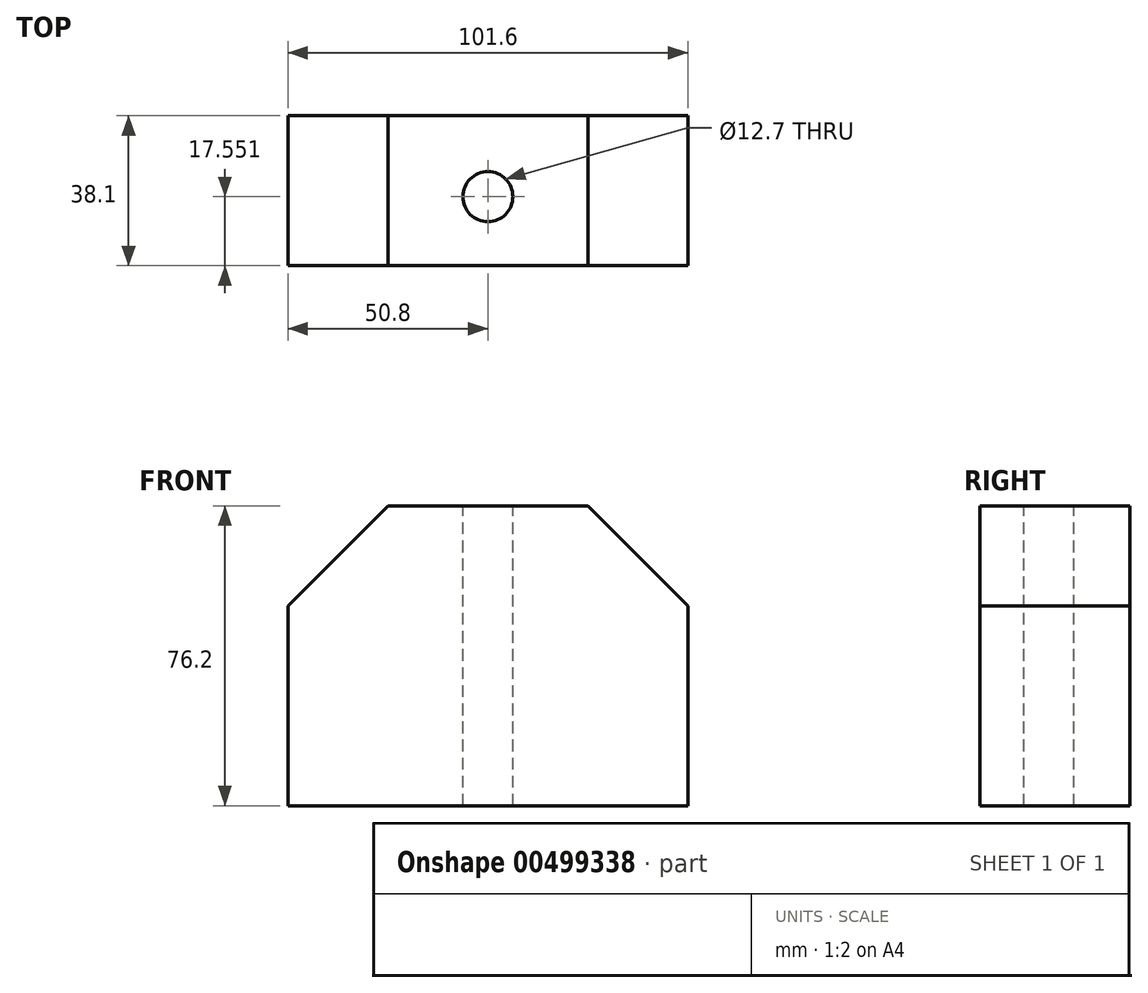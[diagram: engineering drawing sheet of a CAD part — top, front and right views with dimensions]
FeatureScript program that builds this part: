
annotation { "Feature Type Name" : "Feature", "Feature Type Description" : "" }
export const myFeature = defineFeature(function(context is Context, id is Id, definition is map)
    precondition{}
    {
        {
            var Q0;
            Q0=qCreatedBy(makeId("Front.planeOp"),FACE);
            var sketch = newSketch(context, id + "F0", { "sketchPlane" : qUnion([Q0])});
            skLineSegment(sketch, "E0", {"start": v(0, 0) * mm, "end": v(101.6, 0) * mm});
            skLineSegment(sketch, "E1", {"start": v(101.6, 0) * mm, "end": v(101.6, 50.8) * mm});
            skLineSegment(sketch, "E2", {"start": v(101.6, 50.8) * mm, "end": v(76.2, 76.2) * mm});
            skLineSegment(sketch, "E3", {"start": v(76.2, 76.2) * mm, "end": v(25.4, 76.2) * mm});
            skLineSegment(sketch, "E4", {"start": v(25.4, 76.2) * mm, "end": v(0, 50.8) * mm});
            skLineSegment(sketch, "E5", {"start": v(0, 50.8) * mm, "end": v(0, 0) * mm});
            skSolve(sketch);
        }
        {
            var Q0;
            Q0=makeQuery(id+"F0.imprint","IMPRINT",FACE,{"disambiguationData":[TD([[makeQuery(id+"F0.imprint","IMPRINT",EDGE,{"derivedFrom":sQuery(id+"F0.wireOp",EDGE,"E0")}),1.0]])]});
            extrude(context, id + "F1", {"entities" : qUnion([Q0]), "depth" : 38.1 * mm});
        }
        {
            var Q0;
            Q0=makeQuery(id+"F1.opExtrude","SWEPT_FACE",FACE,{"disambiguationData":[OSD([sQuery(id+"F0.wireOp",EDGE,"E3")])]});
            var sketch = newSketch(context, id + "F2", { "sketchPlane" : qUnion([Q0])});
            skLineSegment(sketch, "E6", {"start": v(50.8, -40.37) * mm, "end": v(50.8, -20.55) * mm});
            skPoint(sketch, "E6.startSnap0", {"position": v(50.8, -38.1) * mm});
            skCircle(sketch, "E7", {"center": v(50.8, -20.55) * mm, "radius": 6.35 * mm});
            skSolve(sketch);
        }
        {
            var Q0;
            Q0=makeQuery(id+"F2.imprint","IMPRINT",FACE,{"disambiguationData":[TD([[makeQuery(id+"F2.imprint","IMPRINT",EDGE,{"derivedFrom":sQuery(id+"F2.wireOp",EDGE,"E7")}),1.0]])]});
            extrude(context, id + "F3", {"entities" : qUnion([Q0]), "operationType" : NewBodyOperationType.REMOVE, "endBound" : BoundingType.THROUGH_ALL, "oppositeDirection" : true, "depth" : 25.4 * mm});
        }
    });
